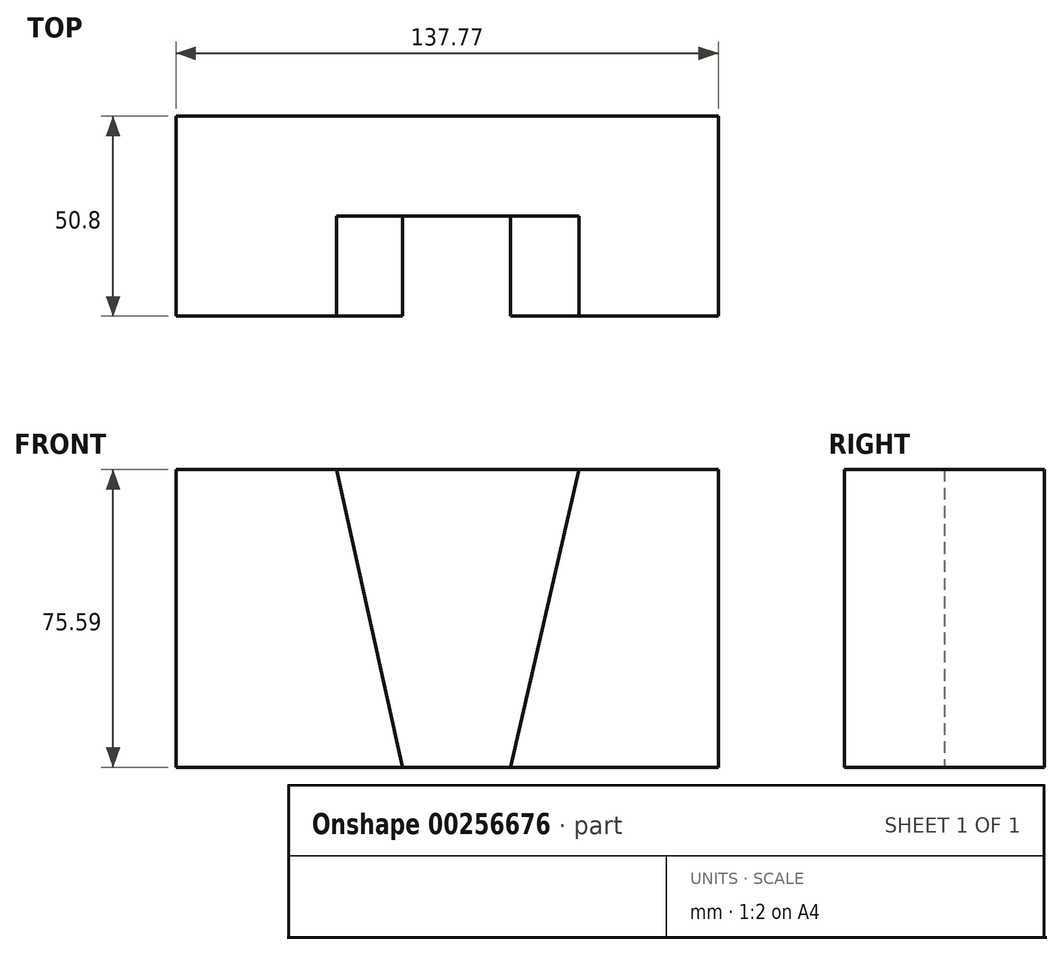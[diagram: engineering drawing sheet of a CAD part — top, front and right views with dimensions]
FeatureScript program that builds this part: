
annotation { "Feature Type Name" : "Feature", "Feature Type Description" : "" }
export const myFeature = defineFeature(function(context is Context, id is Id, definition is map)
    precondition{}
    {
        {
            var Q0;
            Q0=qCreatedBy(makeId("Front.planeOp"),FACE);
            var sketch = newSketch(context, id + "F0", { "sketchPlane" : qUnion([Q0])});
            skLineSegment(sketch, "E0.bottom", {"start": v(-66.14, 31.24) * mm, "end": v(71.63, 31.24) * mm});
            skLineSegment(sketch, "E0.top", {"start": v(-66.14, -44.35) * mm, "end": v(71.63, -44.35) * mm});
            skLineSegment(sketch, "E0.left", {"start": v(-66.14, 31.24) * mm, "end": v(-66.14, -44.35) * mm});
            skLineSegment(sketch, "E0.right", {"start": v(71.63, 31.24) * mm, "end": v(71.63, -44.35) * mm});
            skSolve(sketch);
        }
        {
            var Q0;
            Q0 = qSketchRegion(id + "F0", true);
            extrude(context, id + "F1", {"entities" : qUnion([Q0]), "depth" : 25.4 * mm});
        }
        {
            var Q0;
            Q0=makeQuery(id+"F1.opExtrude","CAP_FACE",FACE,{"disambiguationData":[OSD([sQuery(id+"F0.wireOp",EDGE,"E0.bottom"),sQuery(id+"F0.wireOp",EDGE,"E0.top"),sQuery(id+"F0.wireOp",EDGE,"E0.left"),sQuery(id+"F0.wireOp",EDGE,"E0.right")])],"isStart":false});
            var sketch = newSketch(context, id + "F2", { "sketchPlane" : qUnion([Q0])});
            skLineSegment(sketch, "E1.bottom", {"start": v(-66.14, 31.24) * mm, "end": v(-25.3, 31.24) * mm});
            skLineSegment(sketch, "E1.top", {"start": v(-66.14, -44.35) * mm, "end": v(-25.3, -44.35) * mm});
            skLineSegment(sketch, "E1.left", {"start": v(-66.14, 31.24) * mm, "end": v(-66.14, -44.35) * mm});
            skLineSegment(sketch, "E1.right", {"start": v(-25.3, 31.24) * mm, "end": v(-25.3, -44.35) * mm});
            skLineSegment(sketch, "E2.bottom", {"start": v(71.63, 31.24) * mm, "end": v(36.27, 31.24) * mm});
            skLineSegment(sketch, "E2.top", {"start": v(71.63, -44.35) * mm, "end": v(36.27, -44.35) * mm});
            skLineSegment(sketch, "E2.left", {"start": v(71.63, 31.24) * mm, "end": v(71.63, -44.35) * mm});
            skLineSegment(sketch, "E2.right", {"start": v(36.27, 31.24) * mm, "end": v(36.27, -44.35) * mm});
            skLineSegment(sketch, "E3", {"start": v(-25.3, 31.24) * mm, "end": v(-8.53, -44.35) * mm});
            skLineSegment(sketch, "E4", {"start": v(-8.53, -44.35) * mm, "end": v(-25.3, -44.35) * mm});
            skLineSegment(sketch, "E5", {"start": v(36.27, 31.24) * mm, "end": v(18.9, -44.35) * mm});
            skLineSegment(sketch, "E6", {"start": v(18.9, -44.35) * mm, "end": v(36.27, -44.35) * mm});
            skSolve(sketch);
        }
        {
            var Q0;
            Q0 = qSketchRegion(id + "F2", true);
            extrude(context, id + "F3", {"entities" : qUnion([Q0]), "operationType" : NewBodyOperationType.ADD, "depth" : 25.4 * mm});
        }
    });
